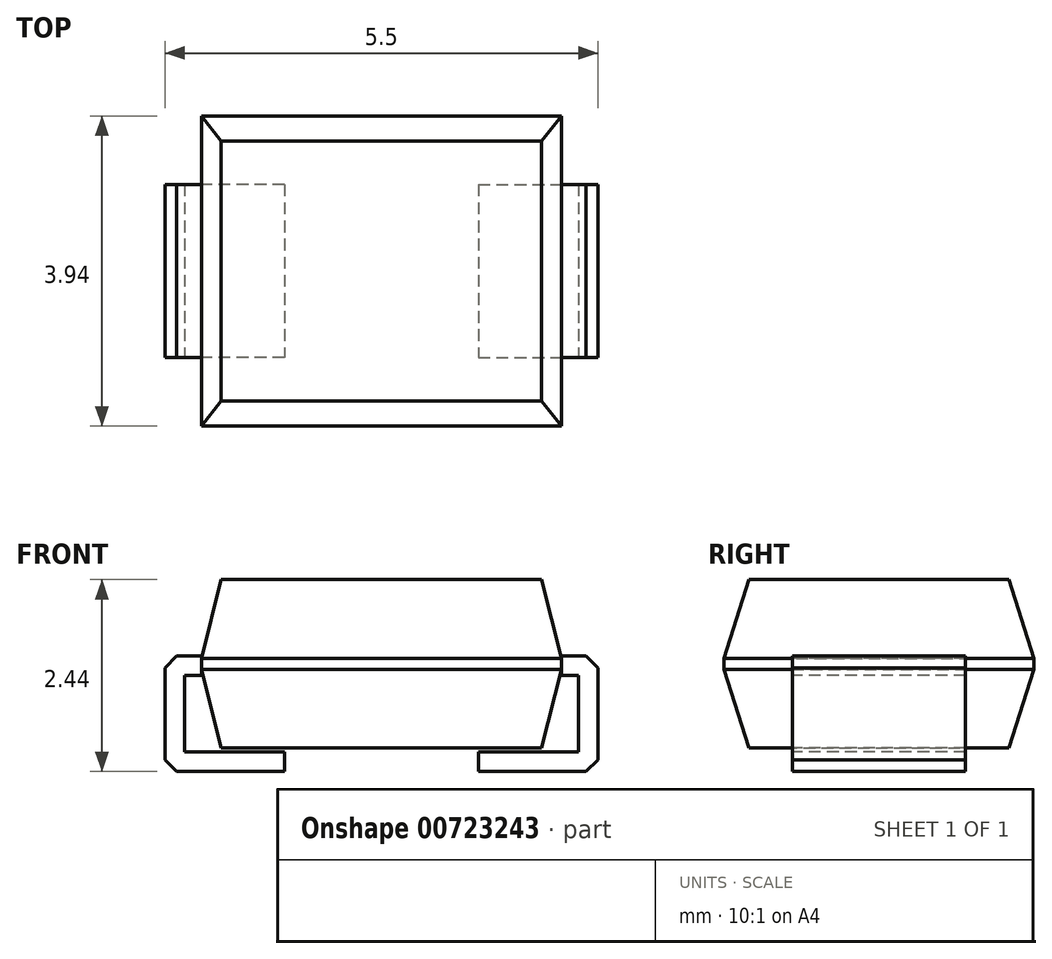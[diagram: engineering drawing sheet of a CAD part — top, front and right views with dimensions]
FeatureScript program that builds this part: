
annotation { "Feature Type Name" : "Feature", "Feature Type Description" : "" }
export const myFeature = defineFeature(function(context is Context, id is Id, definition is map)
    precondition{}
    {
        {
            var Q0;
            Q0=qCreatedBy(makeId("Top.planeOp"),FACE);
            var sketch = newSketch(context, id + "F0", { "sketchPlane" : qUnion([Q0])});
            skLineSegment(sketch, "E0.bottom", {"start": v(-1.23, 1.1) * mm, "end": v(-2.75, 1.1) * mm});
            skLineSegment(sketch, "E0.top", {"start": v(-1.23, -1.1) * mm, "end": v(-2.75, -1.1) * mm});
            skLineSegment(sketch, "E0.left", {"start": v(-1.23, 1.1) * mm, "end": v(-1.23, -1.1) * mm});
            skLineSegment(sketch, "E0.right", {"start": v(-2.75, 1.1) * mm, "end": v(-2.75, -1.1) * mm});
            skPoint(sketch, "E0.middle", {"position": v(-2, 0) * mm});
            skLineSegment(sketch, "E1.MirrorCS", {"start": v(1.23, 1.1) * mm, "end": v(2.75, 1.1) * mm});
            skLineSegment(sketch, "E2.MirrorCS", {"start": v(2.75, 1.1) * mm, "end": v(2.75, -1.1) * mm});
            skLineSegment(sketch, "E3.MirrorCS", {"start": v(1.23, -1.1) * mm, "end": v(2.75, -1.1) * mm});
            skLineSegment(sketch, "E4.MirrorCS", {"start": v(1.23, 1.1) * mm, "end": v(1.23, -1.1) * mm});
            skLineSegment(sketch, "E5", {"start": v(-2.5, 1.1) * mm, "end": v(-2.5, -1.1) * mm});
            skLineSegment(sketch, "E6.MirrorCS", {"start": v(2.5, 1.1) * mm, "end": v(2.5, -1.1) * mm});
            skSolve(sketch);
        }
        {
            var Q0;
            {var subQ0=sQuery(id+"F0.wireOp",EDGE,"E0.left");Q0=makeQuery(id+"F0.imprint","IMPRINT",FACE,{"disambiguationData":[TD([[makeQuery(id+"F0.imprint","IMPRINT",EDGE,{"derivedFrom":subQ0}),-1.0]])]});}
            var Q1;
            {var subQ0=sQuery(id+"F0.wireOp",EDGE,"E4.MirrorCS");Q1=makeQuery(id+"F0.imprint","IMPRINT",FACE,{"disambiguationData":[TD([[makeQuery(id+"F0.imprint","IMPRINT",EDGE,{"derivedFrom":subQ0}),1.0]])]});}
            extrude(context, id + "F1", {"entities" : qUnion([Q0, Q1]), "depth" : 0.25 * mm, "offsetDistance" : 25 * mm});
        }
        {
            var Q0;
            {var subQ0=sQuery(id+"F0.wireOp",EDGE,"E0.right");Q0=makeQuery(id+"F0.imprint","IMPRINT",FACE,{"disambiguationData":[TD([[makeQuery(id+"F0.imprint","IMPRINT",EDGE,{"derivedFrom":subQ0}),1.0]])]});}
            var Q1;
            {var subQ0=sQuery(id+"F0.wireOp",EDGE,"E2.MirrorCS");Q1=makeQuery(id+"F0.imprint","IMPRINT",FACE,{"disambiguationData":[TD([[makeQuery(id+"F0.imprint","IMPRINT",EDGE,{"derivedFrom":subQ0}),-1.0]])]});}
            extrude(context, id + "F2", {"entities" : qUnion([Q0, Q1]), "operationType" : NewBodyOperationType.ADD, "depth" : 1.22 * mm, "offsetDistance" : 25 * mm});
        }
        {
            var Q0;
            Q0=qCreatedBy(makeId("Top.planeOp"),FACE);
            cPlane(context, id + "F3", {"entities" : qUnion([Q0]), "cplaneType" : CPlaneType.OFFSET, "offset" : 0.3 * mm, "width" : 150 * mm, "height" : 150 * mm});
        }
        {
            var Q0;
            Q0=qCreatedBy(id+"F3.planeOp",FACE);
            var sketch = newSketch(context, id + "F4", { "sketchPlane" : qUnion([Q0])});
            skLineSegment(sketch, "E7.bottom", {"start": v(2.28, 1.97) * mm, "end": v(-2.29, 1.97) * mm});
            skLineSegment(sketch, "E7.top", {"start": v(2.29, -1.97) * mm, "end": v(-2.28, -1.97) * mm});
            skLineSegment(sketch, "E7.left", {"start": v(2.28, 1.97) * mm, "end": v(2.29, -1.97) * mm});
            skLineSegment(sketch, "E7.right", {"start": v(-2.29, 1.97) * mm, "end": v(-2.28, -1.97) * mm});
            skPoint(sketch, "E7.middle", {"position": v(0, 0) * mm});
            skSolve(sketch);
        }
        {
            var Q0;
            Q0=makeQuery(id+"F4.imprint","IMPRINT",FACE,{"disambiguationData":[TD([[makeQuery(id+"F4.imprint","IMPRINT",EDGE,{"derivedFrom":sQuery(id+"F4.wireOp",EDGE,"E7.bottom")}),1.0]])]});
            extrude(context, id + "F5", {"entities" : qUnion([Q0]), "depth" : 2.14 * mm, "offsetDistance" : 25 * mm});
        }
        {
            var Q0;
            Q0=makeQuery(id+"F5.opExtrude","CAP_EDGE",EDGE,{"disambiguationData":[OSD([sQuery(id+"F4.wireOp",EDGE,"E7.right")])],"isStart":false});
            var Q1;
            Q1=makeQuery(id+"F5.opExtrude","CAP_EDGE",EDGE,{"disambiguationData":[OSD([sQuery(id+"F4.wireOp",EDGE,"E7.left")])],"isStart":false});
            var Q2;
            Q2=makeQuery(id+"F5.opExtrude","CAP_EDGE",EDGE,{"disambiguationData":[OSD([sQuery(id+"F4.wireOp",EDGE,"E7.right")])],"isStart":true});
            var Q3;
            Q3=makeQuery(id+"F5.opExtrude","CAP_EDGE",EDGE,{"disambiguationData":[OSD([sQuery(id+"F4.wireOp",EDGE,"E7.left")])],"isStart":true});
            chamfer(context, id + "F6", {"entities" : qUnion([Q0, Q1, Q2, Q3]), "chamferType" : ChamferType.TWO_OFFSETS, "width1" : 0.25 * mm, "oppositeDirection" : false, "width2" : 1 * mm, "tangentPropagation" : true});
        }
        {
            var Q0;
            Q0=makeQuery(id+"F5.opExtrude","CAP_EDGE",EDGE,{"disambiguationData":[OSD([sQuery(id+"F4.wireOp",EDGE,"E7.bottom")])],"isStart":false});
            var Q1;
            Q1=makeQuery(id+"F5.opExtrude","CAP_EDGE",EDGE,{"disambiguationData":[OSD([sQuery(id+"F4.wireOp",EDGE,"E7.bottom")])],"isStart":true});
            var Q2;
            Q2=makeQuery(id+"F5.opExtrude","CAP_EDGE",EDGE,{"disambiguationData":[OSD([sQuery(id+"F4.wireOp",EDGE,"E7.top")])],"isStart":false});
            var Q3;
            Q3=makeQuery(id+"F5.opExtrude","CAP_EDGE",EDGE,{"disambiguationData":[OSD([sQuery(id+"F4.wireOp",EDGE,"E7.top")])],"isStart":true});
            chamfer(context, id + "F7", {"entities" : qUnion([Q0, Q1, Q2, Q3]), "chamferType" : ChamferType.TWO_OFFSETS, "width1" : 0.32 * mm, "oppositeDirection" : false, "width2" : 1 * mm, "tangentPropagation" : true});
        }
        {
            var Q0;
            Q0=qCreatedBy(makeId("Top.planeOp"),FACE);
            cPlane(context, id + "F8", {"entities" : qUnion([Q0]), "cplaneType" : CPlaneType.OFFSET, "offset" : 1.22 * mm, "width" : 150 * mm, "height" : 150 * mm});
        }
        {
            var Q0;
            Q0=qCreatedBy(id+"F8.planeOp",FACE);
            var sketch = newSketch(context, id + "F9", { "sketchPlane" : qUnion([Q0])});
            skLineSegment(sketch, "E8", {"start": v(-2.75, 1.1) * mm, "end": v(-2.75, -1.1) * mm});
            skLineSegment(sketch, "E9", {"start": v(-2.29, 1.1) * mm, "end": v(-2.29, -1.1) * mm});
            skLineSegment(sketch, "E10", {"start": v(-2.75, 1.1) * mm, "end": v(-2.29, 1.1) * mm});
            skLineSegment(sketch, "E11", {"start": v(-2.75, -1.1) * mm, "end": v(-2.29, -1.1) * mm});
            skLineSegment(sketch, "E12.MirrorCS", {"start": v(2.75, 1.1) * mm, "end": v(2.29, 1.1) * mm});
            skLineSegment(sketch, "E13.MirrorCS", {"start": v(2.75, 1.1) * mm, "end": v(2.75, -1.1) * mm});
            skLineSegment(sketch, "E14.MirrorCS", {"start": v(2.75, -1.1) * mm, "end": v(2.29, -1.1) * mm});
            skLineSegment(sketch, "E15.MirrorCS", {"start": v(2.29, 1.1) * mm, "end": v(2.29, -1.1) * mm});
            skSolve(sketch);
        }
        {
            var Q0;
            Q0=makeQuery(id+"F9.imprint","IMPRINT",FACE,{"disambiguationData":[TD([[makeQuery(id+"F9.imprint","IMPRINT",EDGE,{"derivedFrom":sQuery(id+"F9.wireOp",EDGE,"E8")}),1.0]])]});
            var Q1;
            Q1=makeQuery(id+"F9.imprint","IMPRINT",FACE,{"disambiguationData":[TD([[makeQuery(id+"F9.imprint","IMPRINT",EDGE,{"derivedFrom":sQuery(id+"F9.wireOp",EDGE,"E12.MirrorCS")}),1.0]])]});
            extrude(context, id + "F10", {"entities" : qUnion([Q0, Q1]), "operationType" : NewBodyOperationType.ADD, "depth" : 0.25 * mm, "offsetDistance" : 25 * mm});
        }
        {
            var Q0;
            Q0=makeQuery(id+"F10.opExtrude","CAP_EDGE",EDGE,{"disambiguationData":[OSD([sQuery(id+"F9.wireOp",EDGE,"E8")])],"isStart":false});
            var Q1;
            Q1=makeQuery(id+"F10.opExtrude","CAP_EDGE",EDGE,{"disambiguationData":[OSD([sQuery(id+"F9.wireOp",EDGE,"E13.MirrorCS")])],"isStart":false});
            var Q2;
            Q2=makeQuery(id+"F2.opExtrude","CAP_EDGE",EDGE,{"disambiguationData":[OSD([sQuery(id+"F0.wireOp",EDGE,"E2.MirrorCS")])],"isStart":true});
            var Q3;
            Q3=makeQuery(id+"F2.opExtrude","CAP_EDGE",EDGE,{"disambiguationData":[OSD([sQuery(id+"F0.wireOp",EDGE,"E0.right")])],"isStart":true});
            chamfer(context, id + "F11", {"entities" : qUnion([Q0, Q1, Q2, Q3]), "width" : 0.15 * mm, "tangentPropagation" : true});
        }
    });
